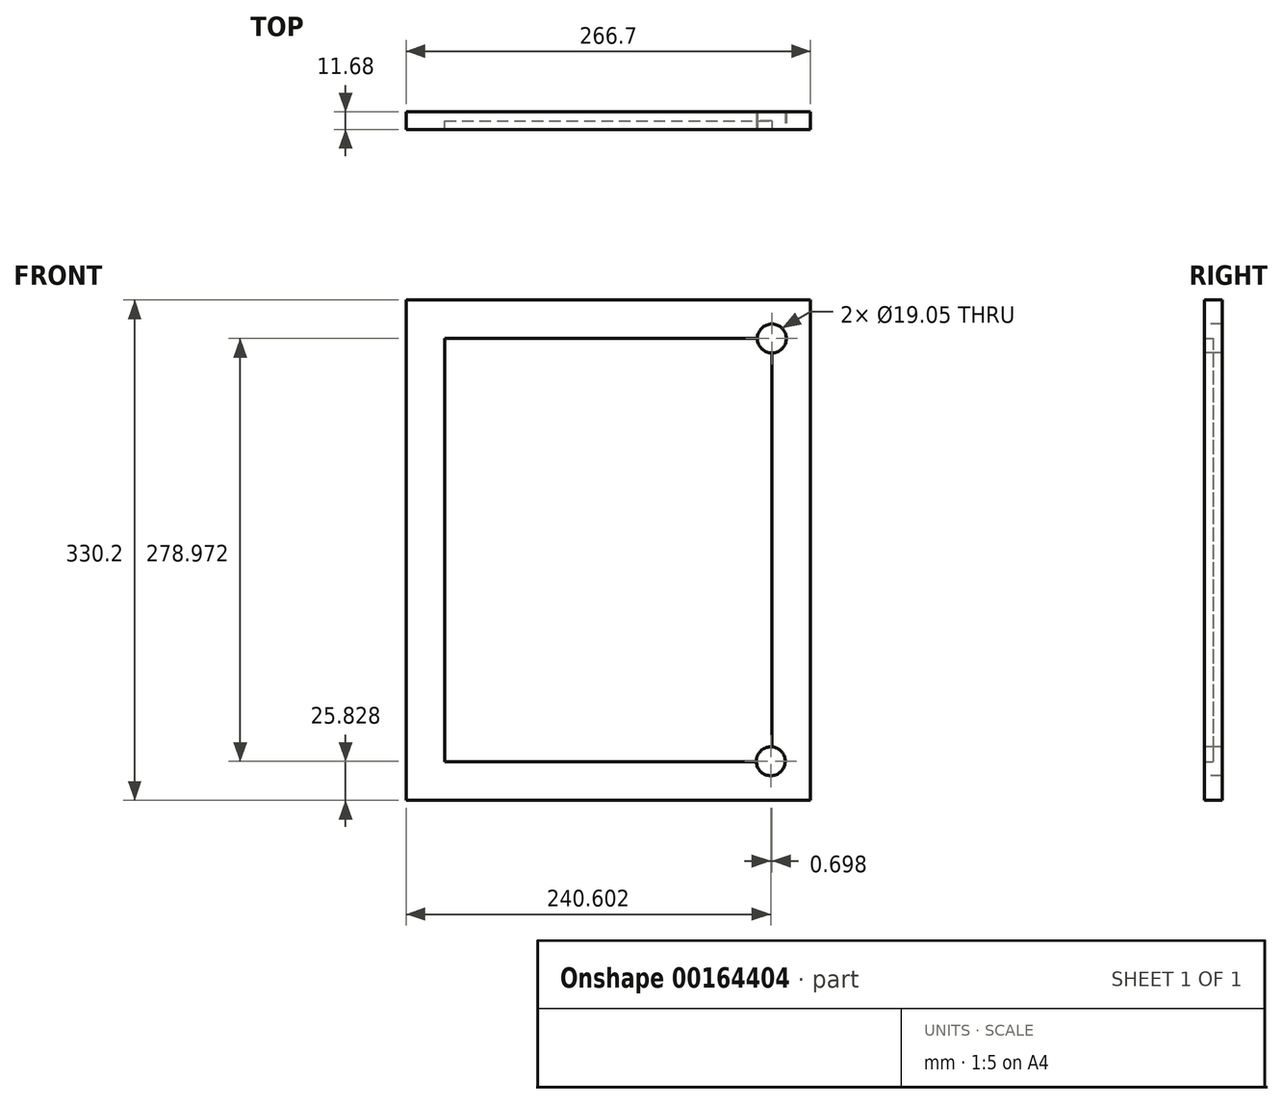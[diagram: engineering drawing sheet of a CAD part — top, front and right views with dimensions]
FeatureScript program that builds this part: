
annotation { "Feature Type Name" : "Feature", "Feature Type Description" : "" }
export const myFeature = defineFeature(function(context is Context, id is Id, definition is map)
    precondition{}
    {
        {
            var Q0;
            Q0=qCreatedBy(makeId("Front.planeOp"),FACE);
            var sketch = newSketch(context, id + "F0", { "sketchPlane" : qUnion([Q0])});
            skLineSegment(sketch, "E0.bottom", {"start": v(0, 330.2) * mm, "end": v(266.7, 330.2) * mm});
            skLineSegment(sketch, "E0.top", {"start": v(0, 0) * mm, "end": v(266.7, 0) * mm});
            skLineSegment(sketch, "E0.left", {"start": v(0, 330.2) * mm, "end": v(0, 0) * mm});
            skLineSegment(sketch, "E0.right", {"start": v(266.7, 330.2) * mm, "end": v(266.7, 0) * mm});
            skSolve(sketch);
        }
        {
            var Q0;
            Q0=makeQuery(id+"F0.imprint","IMPRINT",FACE,{"disambiguationData":[TD([[makeQuery(id+"F0.imprint","IMPRINT",EDGE,{"derivedFrom":sQuery(id+"F0.wireOp",EDGE,"E0.bottom")}),-1.0]])]});
            extrude(context, id + "F1", {"entities" : qUnion([Q0]), "depth" : 5.84 * mm});
        }
        {
            var Q0;
            Q0=makeQuery(id+"F1.opExtrude","CAP_FACE",FACE,{"disambiguationData":[OSD([sQuery(id+"F0.wireOp",EDGE,"E0.bottom"),sQuery(id+"F0.wireOp",EDGE,"E0.top"),sQuery(id+"F0.wireOp",EDGE,"E0.left"),sQuery(id+"F0.wireOp",EDGE,"E0.right")])],"isStart":false});
            var sketch = newSketch(context, id + "F2", { "sketchPlane" : qUnion([Q0])});
            skLineSegment(sketch, "E1.bottom", {"start": v(25.4, 304.8) * mm, "end": v(241.3, 304.8) * mm});
            skLineSegment(sketch, "E1.top", {"start": v(25.4, 25.4) * mm, "end": v(241.3, 25.4) * mm});
            skLineSegment(sketch, "E1.left", {"start": v(25.4, 304.8) * mm, "end": v(25.4, 25.4) * mm});
            skLineSegment(sketch, "E1.right", {"start": v(241.3, 304.8) * mm, "end": v(241.3, 25.4) * mm});
            skSolve(sketch);
        }
        {
            var Q0;
            Q0=makeQuery(id+"F2.imprint","IMPRINT",FACE,{"disambiguationData":[TD([[makeQuery(id+"F2.imprint","IMPRINT",EDGE,{"derivedFrom":sQuery(id+"F2.wireOp",EDGE,"E1.bottom")}),1.0]])]});
            extrude(context, id + "F3", {"entities" : qUnion([Q0]), "depth" : 5.84 * mm});
        }
        {
            var Q0;
            Q0=makeQuery(id+"F1.opExtrude","SWEPT_BODY",BODY,{"disambiguationData":[OSD([sQuery(id+"F0.wireOp",EDGE,"E0.bottom"),sQuery(id+"F0.wireOp",EDGE,"E0.top"),sQuery(id+"F0.wireOp",EDGE,"E0.left"),sQuery(id+"F0.wireOp",EDGE,"E0.right")])]});
            var Q1;
            Q1=makeQuery(id+"F3.opExtrude","SWEPT_BODY",BODY,{"disambiguationData":[OSD([sQuery(id+"F0.wireOp",EDGE,"E0.bottom"),sQuery(id+"F0.wireOp",EDGE,"E0.top"),sQuery(id+"F0.wireOp",EDGE,"E0.left"),sQuery(id+"F0.wireOp",EDGE,"E0.right"),sQuery(id+"F2.wireOp",EDGE,"E1.bottom"),sQuery(id+"F2.wireOp",EDGE,"E1.top"),sQuery(id+"F2.wireOp",EDGE,"E1.left"),sQuery(id+"F2.wireOp",EDGE,"E1.right")])]});
            booleanBodies(context, id + "F4", {"operationType" : BooleanOperationType.UNION, "tools" : qUnion([Q0, Q1])});
        }
        {
            var Q0;
            Q0=makeQuery(id+"F3.opExtrude","CAP_FACE",FACE,{"disambiguationData":[OSD([sQuery(id+"F0.wireOp",EDGE,"E0.bottom"),sQuery(id+"F0.wireOp",EDGE,"E0.top"),sQuery(id+"F0.wireOp",EDGE,"E0.left"),sQuery(id+"F0.wireOp",EDGE,"E0.right"),sQuery(id+"F2.wireOp",EDGE,"E1.bottom"),sQuery(id+"F2.wireOp",EDGE,"E1.top"),sQuery(id+"F2.wireOp",EDGE,"E1.left"),sQuery(id+"F2.wireOp",EDGE,"E1.right")])],"isStart":false});
            var sketch = newSketch(context, id + "F5", { "sketchPlane" : qUnion([Q0])});
            skLineSegment(sketch, "E2", {"start": v(-19.05, 165.1) * mm, "end": v(25.4, 165.1) * mm});
            skLineSegment(sketch, "E3", {"start": v(133.35, 330.2) * mm, "end": v(133.35, 0) * mm});
            skLineSegment(sketch, "E4", {"start": v(0, 203.2) * mm, "end": v(25.4, 203.2) * mm});
            skLineSegment(sketch, "E5", {"start": v(0, 190.5) * mm, "end": v(25.4, 190.5) * mm});
            skLineSegment(sketch, "E6", {"start": v(0, 177.8) * mm, "end": v(25.4, 177.8) * mm});
            skPoint(sketch, "E7", {"position": v(133.35, 165.1) * mm});
            skLineSegment(sketch, "E8", {"start": v(0, 127) * mm, "end": v(25.4, 127) * mm});
            skLineSegment(sketch, "E9", {"start": v(0, 139.7) * mm, "end": v(25.4, 139.7) * mm});
            skLineSegment(sketch, "E10", {"start": v(0, 152.4) * mm, "end": v(25.4, 152.4) * mm});
            skPoint(sketch, "E11", {"position": v(25.4, 203.2) * mm});
            skPoint(sketch, "E12", {"position": v(25.4, 190.5) * mm});
            skPoint(sketch, "E13", {"position": v(25.4, 177.8) * mm});
            skPoint(sketch, "E14", {"position": v(25.4, 165.1) * mm});
            skPoint(sketch, "E15", {"position": v(25.4, 152.4) * mm});
            skPoint(sketch, "E16", {"position": v(25.4, 139.7) * mm});
            skPoint(sketch, "E17", {"position": v(25.4, 127) * mm});
            skPoint(sketch, "E18", {"position": v(241.3, 127) * mm});
            skPoint(sketch, "E19", {"position": v(241.3, 139.7) * mm});
            skPoint(sketch, "E20", {"position": v(241.3, 152.4) * mm});
            skPoint(sketch, "E21", {"position": v(241.3, 165.1) * mm});
            skPoint(sketch, "E22", {"position": v(241.3, 177.8) * mm});
            skPoint(sketch, "E23", {"position": v(241.3, 190.5) * mm});
            skPoint(sketch, "E24", {"position": v(241.3, 203.2) * mm});
            skLineSegment(sketch, "E25.trimOffspring", {"start": v(241.3, 203.2) * mm, "end": v(266.7, 203.2) * mm});
            skLineSegment(sketch, "E26.trimOffspring", {"start": v(241.3, 190.5) * mm, "end": v(266.7, 190.5) * mm});
            skLineSegment(sketch, "E27.trimOffspring", {"start": v(241.3, 177.8) * mm, "end": v(266.7, 177.8) * mm});
            skLineSegment(sketch, "E28.trimOffspring", {"start": v(241.3, 165.1) * mm, "end": v(285.75, 165.1) * mm});
            skLineSegment(sketch, "E29.trimOffspring", {"start": v(241.3, 152.4) * mm, "end": v(266.7, 152.4) * mm});
            skLineSegment(sketch, "E30.trimOffspring", {"start": v(241.3, 139.7) * mm, "end": v(266.7, 139.7) * mm});
            skLineSegment(sketch, "E31.trimOffspring", {"start": v(241.3, 127) * mm, "end": v(266.7, 127) * mm});
            skLineSegment(sketch, "E32", {"start": v(60.33, 25.4) * mm, "end": v(60.33, 0) * mm});
            skLineSegment(sketch, "E33", {"start": v(63.5, 25.4) * mm, "end": v(63.5, 0) * mm});
            skLineSegment(sketch, "E34", {"start": v(66.68, 25.4) * mm, "end": v(66.68, 0) * mm});
            skLineSegment(sketch, "E35", {"start": v(98.43, 25.4) * mm, "end": v(98.43, 0) * mm});
            skLineSegment(sketch, "E36", {"start": v(95.25, 25.4) * mm, "end": v(95.25, 0) * mm});
            skLineSegment(sketch, "E37", {"start": v(92.08, 25.4) * mm, "end": v(92.08, 0) * mm});
            skLineSegment(sketch, "E38", {"start": v(0, 292.1) * mm, "end": v(25.4, 292.1) * mm});
            skLineSegment(sketch, "E39", {"start": v(0, 298.45) * mm, "end": v(25.4, 298.45) * mm});
            skPoint(sketch, "E40", {"position": v(25.4, 292.1) * mm});
            skPoint(sketch, "E41", {"position": v(25.4, 298.45) * mm});
            skSolve(sketch);
        }
        {
            var Q0;
            Q0=makeQuery(id+"F5.imprint","IMPRINT",FACE,{"disambiguationData":[TD([[makeQuery(id+"F5.imprint","IMPRINT",EDGE,{"derivedFrom":makeQuery(id+"F3.opExtrude","CAP_EDGE",EDGE,{"disambiguationData":[OSD([sQuery(id+"F2.wireOp",EDGE,"E1.bottom")])],"isStart":false})}),1.0]])]});
            var sketch = newSketch(context, id + "F6", { "sketchPlane" : qUnion([Q0])});
            skCircle(sketch, "E42", {"center": v(241.3, 304.8) * mm, "radius": 9.53 * mm});
            skCircle(sketch, "E43", {"center": v(240.6, 25.83) * mm, "radius": 9.52 * mm});
            skSolve(sketch);
        }
        {
            var Q0;
            Q0 = qSketchRegion(id + "F6", true);
            extrude(context, id + "F7", {"entities" : qUnion([Q0]), "operationType" : NewBodyOperationType.REMOVE, "endBound" : BoundingType.THROUGH_ALL, "oppositeDirection" : true, "depth" : 25.4 * mm});
        }
    });
